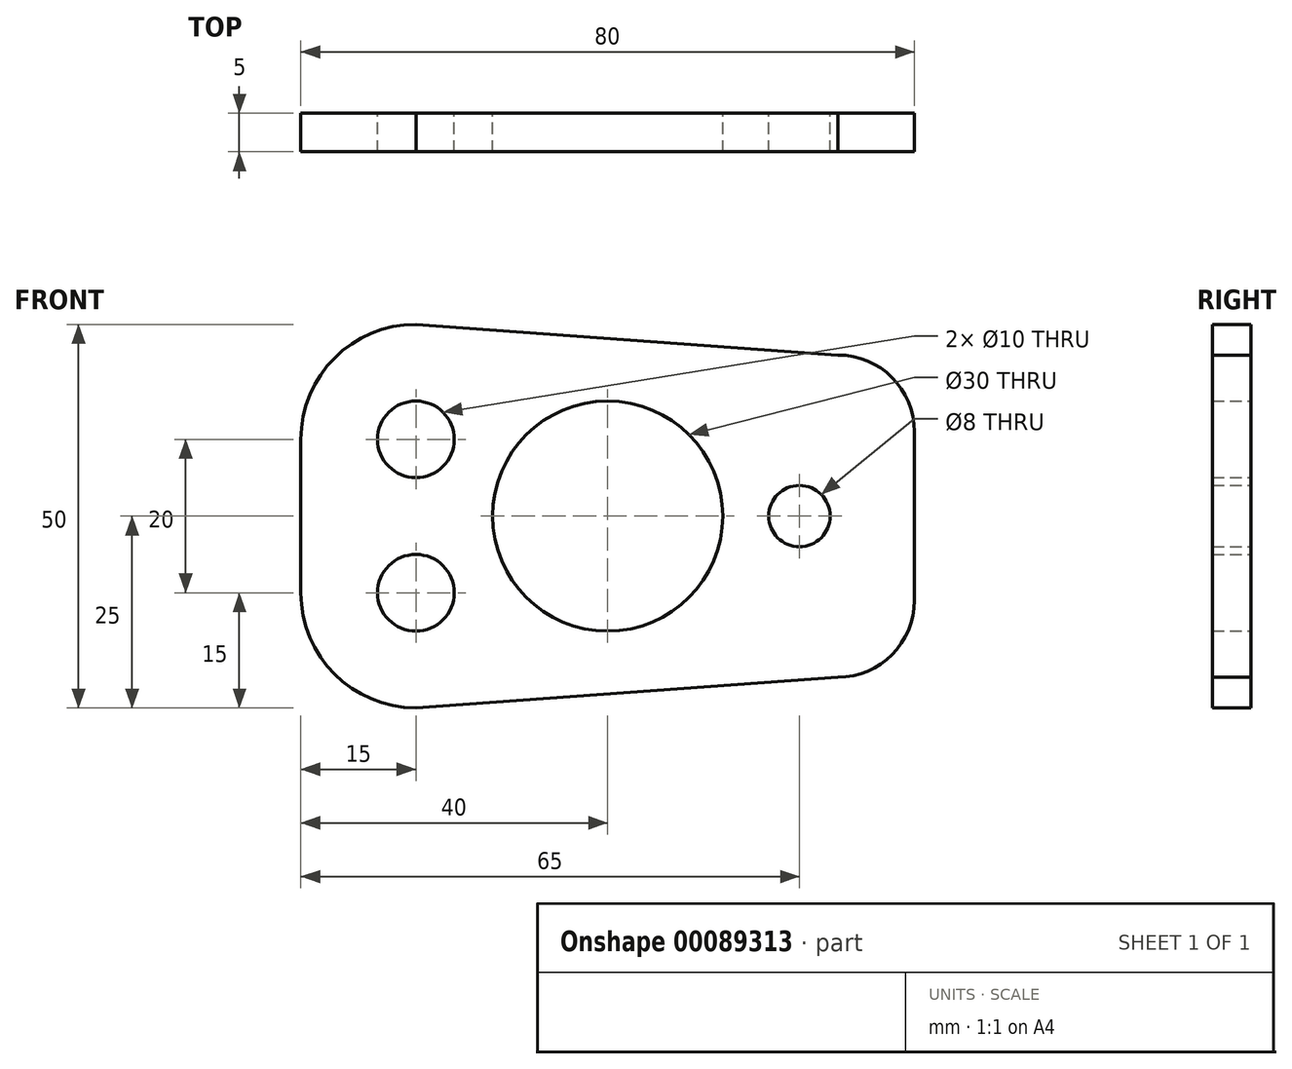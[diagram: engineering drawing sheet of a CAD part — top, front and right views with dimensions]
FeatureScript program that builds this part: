
annotation { "Feature Type Name" : "Feature", "Feature Type Description" : "" }
export const myFeature = defineFeature(function(context is Context, id is Id, definition is map)
    precondition{}
    {
        {
            var Q0;
            Q0=qCreatedBy(makeId("Front.planeOp"),FACE);
            var sketch = newSketch(context, id + "F0", { "sketchPlane" : qUnion([Q0])});
            skCircle(sketch, "E0", {"center": v(0, 0) * mm, "radius": 15 * mm});
            skCircle(sketch, "E1", {"center": v(-25, 10) * mm, "radius": 5 * mm});
            skCircle(sketch, "E2", {"center": v(-25, -10) * mm, "radius": 5 * mm});
            skCircle(sketch, "E3", {"center": v(25, 0) * mm, "radius": 4 * mm});
            skArc(sketch, "E4", {"start": v(-40, 10) * mm, "mid": v(-35.6, 20.6) * mm, "end": v(-25, 25) * mm});
            skArc(sketch, "E5", {"start": v(-40, -10) * mm, "mid": v(-35.6, -20.6) * mm, "end": v(-25, -25) * mm});
            skLineSegment(sketch, "E6", {"start": v(-40, 10) * mm, "end": v(-40, 0) * mm});
            skLineSegment(sketch, "E7", {"start": v(-40, 0) * mm, "end": v(-40, -10) * mm});
            skArc(sketch, "E8", {"start": v(30, 21) * mm, "mid": v(37.07, 18.07) * mm, "end": v(40, 11) * mm});
            skArc(sketch, "E9", {"start": v(40, -11) * mm, "mid": v(37.07, -18.07) * mm, "end": v(30, -21) * mm});
            skLineSegment(sketch, "E10", {"start": v(40, 11) * mm, "end": v(40, 0) * mm});
            skLineSegment(sketch, "E11", {"start": v(40, 0) * mm, "end": v(40, -11) * mm});
            skLineSegment(sketch, "E12", {"start": v(30, -21) * mm, "end": v(-25, -25) * mm});
            skLineSegment(sketch, "E13", {"start": v(-25, 25) * mm, "end": v(30, 21) * mm});
            skSolve(sketch);
        }
        {
            var Q0;
            Q0 = qSketchRegion(id + "F0", true);
            extrude(context, id + "F1", {"entities" : qUnion([Q0]), "depth" : 5 * mm});
        }
    });
